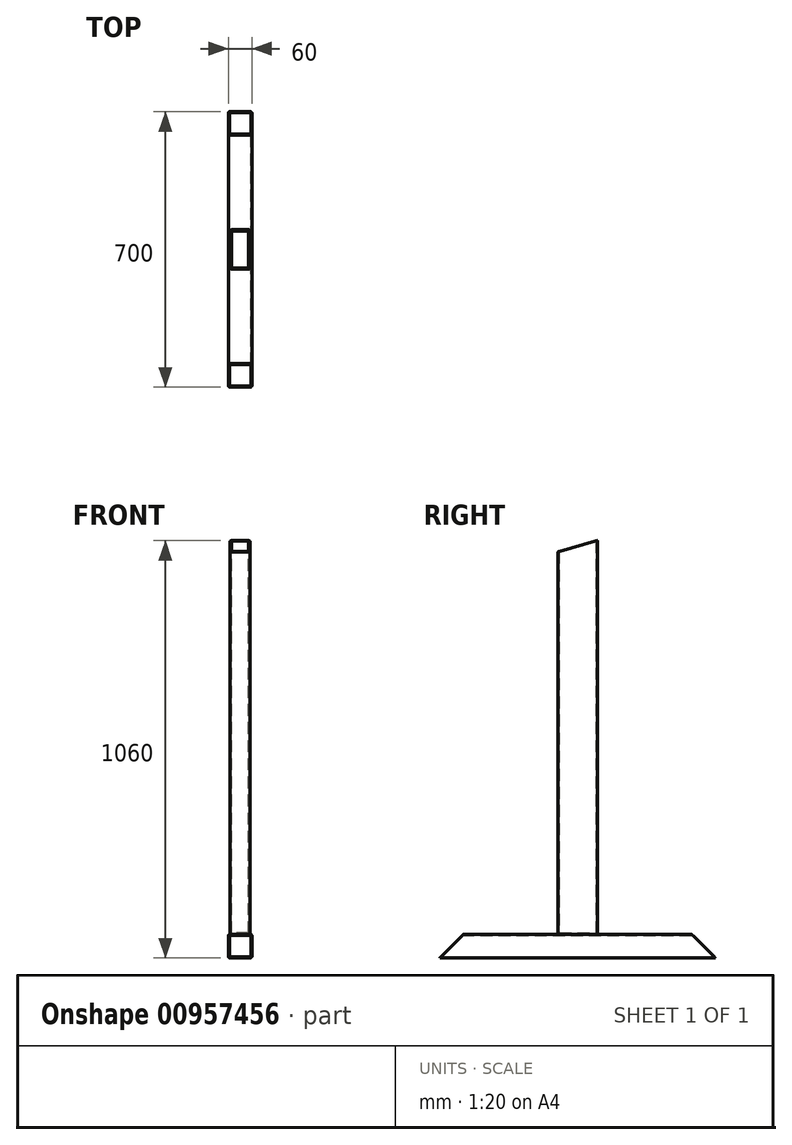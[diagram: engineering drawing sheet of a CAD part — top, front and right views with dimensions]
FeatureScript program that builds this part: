
annotation { "Feature Type Name" : "Feature", "Feature Type Description" : "" }
export const myFeature = defineFeature(function(context is Context, id is Id, definition is map)
    precondition{}
    {
        {
            var Q0;
            Q0=qCreatedBy(makeId("Top.planeOp"),FACE);
            var sketch = newSketch(context, id + "F0", { "sketchPlane" : qUnion([Q0])});
            skLineSegment(sketch, "E0.bottom", {"start": v(0, -848.28) * mm, "end": v(60, -848.28) * mm});
            skLineSegment(sketch, "E0.top", {"start": v(0, -148.28) * mm, "end": v(60, -148.28) * mm});
            skLineSegment(sketch, "E0.left", {"start": v(0, -848.28) * mm, "end": v(0, -148.28) * mm});
            skLineSegment(sketch, "E0.right", {"start": v(60, -848.28) * mm, "end": v(60, -148.28) * mm});
            skSolve(sketch);
        }
        {
            var Q0;
            Q0 = qSketchRegion(id + "F0", true);
            extrude(context, id + "F1", {"entities" : qUnion([Q0]), "depth" : 60 * mm, "offsetDistance" : 25 * mm});
        }
        {
            var Q0;
            Q0=makeQuery(id+"F1.opExtrude","SWEPT_FACE",FACE,{"disambiguationData":[OSD([sQuery(id+"F0.wireOp",EDGE,"E0.bottom")])]});
            var Q1;
            Q1=makeQuery(id+"F1.opExtrude","SWEPT_FACE",FACE,{"disambiguationData":[OSD([sQuery(id+"F0.wireOp",EDGE,"E0.top")])]});
            shell(context, id + "F2", {"entities" : qUnion([Q0, Q1]), "thickness" : 2.5 * mm});
        }
        {
            var Q0;
            Q0=makeQuery(id+"F1.opExtrude","CAP_FACE",FACE,{"disambiguationData":[OSD([sQuery(id+"F0.wireOp",EDGE,"E0.bottom"),sQuery(id+"F0.wireOp",EDGE,"E0.top"),sQuery(id+"F0.wireOp",EDGE,"E0.left"),sQuery(id+"F0.wireOp",EDGE,"E0.right")])],"isStart":false});
            var sketch = newSketch(context, id + "F3", { "sketchPlane" : qUnion([Q0])});
            skLineSegment(sketch, "E1.bottom", {"start": v(55, -548.28) * mm, "end": v(5, -548.28) * mm});
            skLineSegment(sketch, "E1.top", {"start": v(55, -448.28) * mm, "end": v(5, -448.28) * mm});
            skLineSegment(sketch, "E1.left", {"start": v(55, -548.28) * mm, "end": v(55, -448.28) * mm});
            skLineSegment(sketch, "E1.right", {"start": v(5, -548.28) * mm, "end": v(5, -448.28) * mm});
            skPoint(sketch, "E1.middle", {"position": v(30, -498.28) * mm});
            skPoint(sketch, "E1.middle.positionSnap0", {"position": v(0, -498.28) * mm});
            skPoint(sketch, "E1.centerSnap0", {"position": v(0, -498.28) * mm});
            skSolve(sketch);
        }
        {
            var Q0;
            Q0=makeQuery(id+"F3.imprint","IMPRINT",FACE,{"disambiguationData":[TD([[makeQuery(id+"F3.imprint","IMPRINT",EDGE,{"derivedFrom":sQuery(id+"F3.wireOp",EDGE,"E1.bottom")}),-1.0]])]});
            extrude(context, id + "F4", {"entities" : qUnion([Q0]), "depth" : 1000 * mm, "offsetDistance" : 25 * mm});
        }
        {
            var Q0;
            Q0=makeQuery(id+"F1.opExtrude","CAP_EDGE",EDGE,{"disambiguationData":[OSD([sQuery(id+"F0.wireOp",EDGE,"E0.bottom")])],"isStart":false});
            var Q1;
            Q1=makeQuery(id+"F1.opExtrude","CAP_EDGE",EDGE,{"disambiguationData":[OSD([sQuery(id+"F0.wireOp",EDGE,"E0.top")])],"isStart":false});
            chamfer(context, id + "F5", {"entities" : qUnion([Q0, Q1]), "width" : 60 * mm, "tangentPropagation" : true});
        }
        {
            var Q0;
            Q0=makeQuery(id+"F1.opExtrude","CAP_EDGE",EDGE,{"disambiguationData":[OSD([sQuery(id+"F0.wireOp",EDGE,"E0.left")])],"isStart":true});
            var Q1;
            Q1=makeQuery(id+"F1.opExtrude","CAP_EDGE",EDGE,{"disambiguationData":[OSD([sQuery(id+"F0.wireOp",EDGE,"E0.right")])],"isStart":true});
            var Q2;
            Q2=makeQuery(id+"F1.opExtrude","CAP_EDGE",EDGE,{"disambiguationData":[OSD([sQuery(id+"F0.wireOp",EDGE,"E0.right")])],"isStart":false});
            var Q3;
            Q3=makeQuery(id+"F1.opExtrude","CAP_EDGE",EDGE,{"disambiguationData":[OSD([sQuery(id+"F0.wireOp",EDGE,"E0.left")])],"isStart":false});
            var Q4;
            Q4=makeQuery(id+"F4.opExtrude","SWEPT_EDGE",EDGE,{"disambiguationData":[OSD([sQuery(id+"F3.wireOp",EDGE,"E1.bottom"),sQuery(id+"F3.wireOp",EDGE,"E1.left")])]});
            var Q5;
            Q5=makeQuery(id+"F4.opExtrude","SWEPT_EDGE",EDGE,{"disambiguationData":[OSD([sQuery(id+"F3.wireOp",EDGE,"E1.top"),sQuery(id+"F3.wireOp",EDGE,"E1.left")])]});
            var Q6;
            Q6=makeQuery(id+"F4.opExtrude","SWEPT_EDGE",EDGE,{"disambiguationData":[OSD([sQuery(id+"F3.wireOp",EDGE,"E1.top"),sQuery(id+"F3.wireOp",EDGE,"E1.right")])]});
            var Q7;
            Q7=makeQuery(id+"F4.opExtrude","SWEPT_EDGE",EDGE,{"disambiguationData":[OSD([sQuery(id+"F3.wireOp",EDGE,"E1.bottom"),sQuery(id+"F3.wireOp",EDGE,"E1.right")])]});
            fillet(context, id + "F6", {"entities" : qUnion([Q0, Q1, Q2, Q3, Q4, Q5, Q6, Q7]), "radius" : 4 * mm, "tangentPropagation" : true, "allowEdgeOverflow" : false});
        }
        {
            var Q0;
            Q0=makeQuery(id+"F4.opExtrude","CAP_FACE",FACE,{"disambiguationData":[OSD([sQuery(id+"F3.wireOp",EDGE,"E1.bottom"),sQuery(id+"F3.wireOp",EDGE,"E1.top"),sQuery(id+"F3.wireOp",EDGE,"E1.left"),sQuery(id+"F3.wireOp",EDGE,"E1.right")])],"isStart":false});
            shell(context, id + "F7", {"entities" : qUnion([Q0]), "thickness" : 3 * mm});
        }
        {
            var Q0;
            Q0=makeQuery(id+"F4.opExtrude","CAP_EDGE",EDGE,{"disambiguationData":[OSD([sQuery(id+"F3.wireOp",EDGE,"E1.bottom")])],"isStart":false});
            chamfer(context, id + "F8", {"entities" : qUnion([Q0]), "chamferType" : ChamferType.OFFSET_ANGLE, "width" : 100 * mm, "oppositeDirection" : true, "angle" : 16 * degree});
        }
    });
